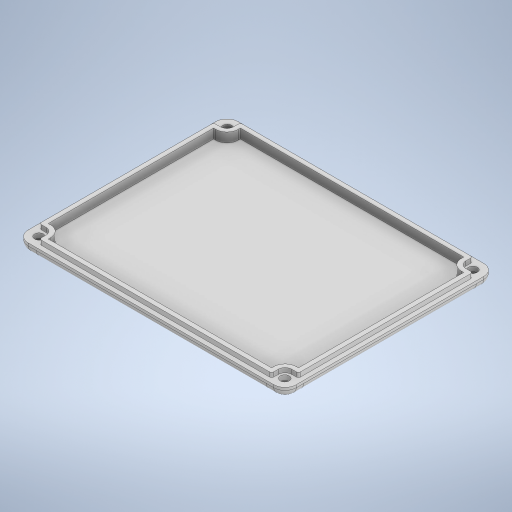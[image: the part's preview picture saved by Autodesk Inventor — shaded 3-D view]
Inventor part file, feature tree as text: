
AUTODESK INVENTOR PART (.ipt)
format: ipt  version: 2024 (Build 280153000, 153)  size: 361,472 bytes
history: native  units: mm
features: extrude x3, sketch x1, chamfer x1, fillet x1
ambient origin geometry x8: Origin, YZ Plane, XZ Plane, XY Plane, X Axis, Y Axis, Z Axis, Center Point
bodies: Solide1 (feature_tree)
feature tree (6):
  sketch  "Esquisse1"
  extrude  "Extrusion1"  Depth=2.0mm
  extrude  "Extrusion2"  Depth=2.0mm TaperAngle=0.0deg
  extrude  "Extrusion3"  Depth=6.2mm TaperAngle=0.0deg
  chamfer  "Chanfrein1"  Distance=4.2mm
  fillet  "Congé1"  Radius=2.0mm
